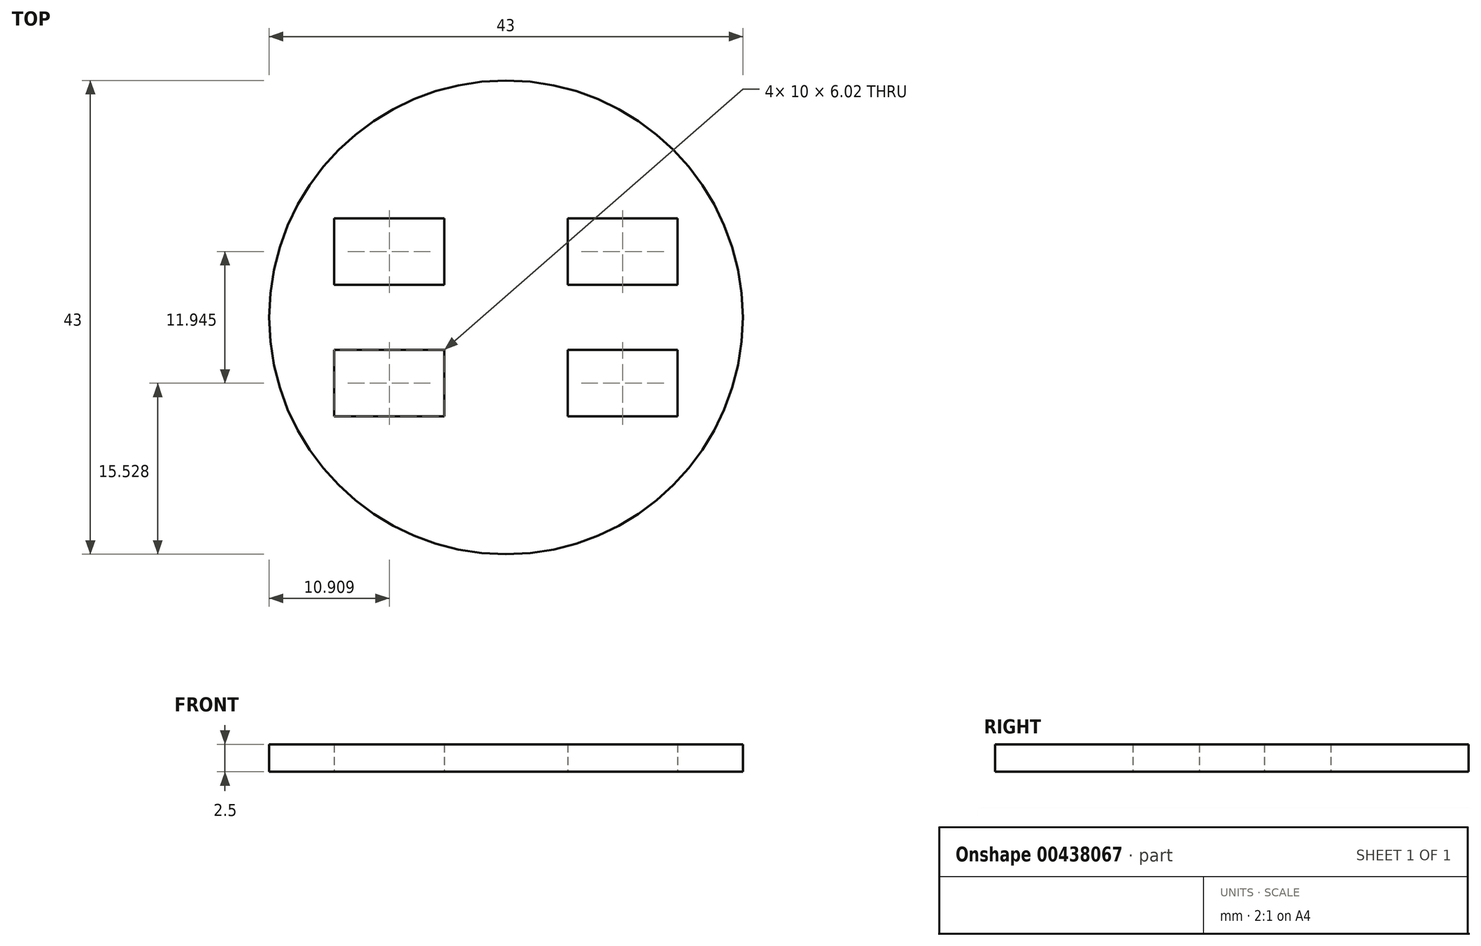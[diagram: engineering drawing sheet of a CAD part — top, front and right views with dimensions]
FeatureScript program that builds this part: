
annotation { "Feature Type Name" : "Feature", "Feature Type Description" : "" }
export const myFeature = defineFeature(function(context is Context, id is Id, definition is map)
    precondition{}
    {
        {
            var Q0;
            Q0=qCreatedBy(makeId("Top.planeOp"),FACE);
            var sketch = newSketch(context, id + "F0", { "sketchPlane" : qUnion([Q0])});
            skCircle(sketch, "E0", {"center": v(0, 0) * mm, "radius": 21.5 * mm});
            skLineSegment(sketch, "E1.bottom", {"start": v(-15.6, 8.98) * mm, "end": v(-5.6, 8.98) * mm});
            skLineSegment(sketch, "E1.top", {"start": v(-15.6, 2.96) * mm, "end": v(-5.6, 2.96) * mm});
            skLineSegment(sketch, "E1.left", {"start": v(-15.6, 8.98) * mm, "end": v(-15.6, 2.96) * mm});
            skLineSegment(sketch, "E1.right", {"start": v(-5.6, 8.98) * mm, "end": v(-5.6, 2.96) * mm});
            skLineSegment(sketch, "E2.MirrorCS", {"start": v(5.6, 8.98) * mm, "end": v(5.6, 2.96) * mm});
            skLineSegment(sketch, "E3.MirrorCS", {"start": v(15.6, 8.98) * mm, "end": v(5.6, 8.98) * mm});
            skLineSegment(sketch, "E4.MirrorCS", {"start": v(15.6, 2.96) * mm, "end": v(5.6, 2.96) * mm});
            skLineSegment(sketch, "E5.MirrorCS", {"start": v(15.6, 8.98) * mm, "end": v(15.6, 2.96) * mm});
            skLineSegment(sketch, "E6.MirrorCS", {"start": v(-15.6, -2.96) * mm, "end": v(-5.6, -2.96) * mm});
            skLineSegment(sketch, "E7.MirrorCS", {"start": v(-5.6, -8.98) * mm, "end": v(-5.6, -2.96) * mm});
            skLineSegment(sketch, "E8.MirrorCS", {"start": v(-15.6, -8.98) * mm, "end": v(-15.6, -2.96) * mm});
            skLineSegment(sketch, "E9.MirrorCS", {"start": v(-15.6, -8.98) * mm, "end": v(-5.6, -8.98) * mm});
            skLineSegment(sketch, "E10.MirrorCS", {"start": v(15.6, -2.96) * mm, "end": v(5.6, -2.96) * mm});
            skLineSegment(sketch, "E11.MirrorCS", {"start": v(5.6, -8.98) * mm, "end": v(5.6, -2.96) * mm});
            skLineSegment(sketch, "E12.MirrorCS", {"start": v(15.6, -8.98) * mm, "end": v(5.6, -8.98) * mm});
            skLineSegment(sketch, "E13.MirrorCS", {"start": v(15.6, -8.98) * mm, "end": v(15.6, -2.96) * mm});
            skSolve(sketch);
        }
        {
            var Q0;
            Q0=makeQuery(id+"F0.imprint","IMPRINT",FACE,{"disambiguationData":[TD([[makeQuery(id+"F0.imprint","IMPRINT",EDGE,{"derivedFrom":sQuery(id+"F0.wireOp",EDGE,"E0")}),1.0]])]});
            extrude(context, id + "F1", {"entities" : qUnion([Q0]), "depth" : 2.5 * mm});
        }
    });
